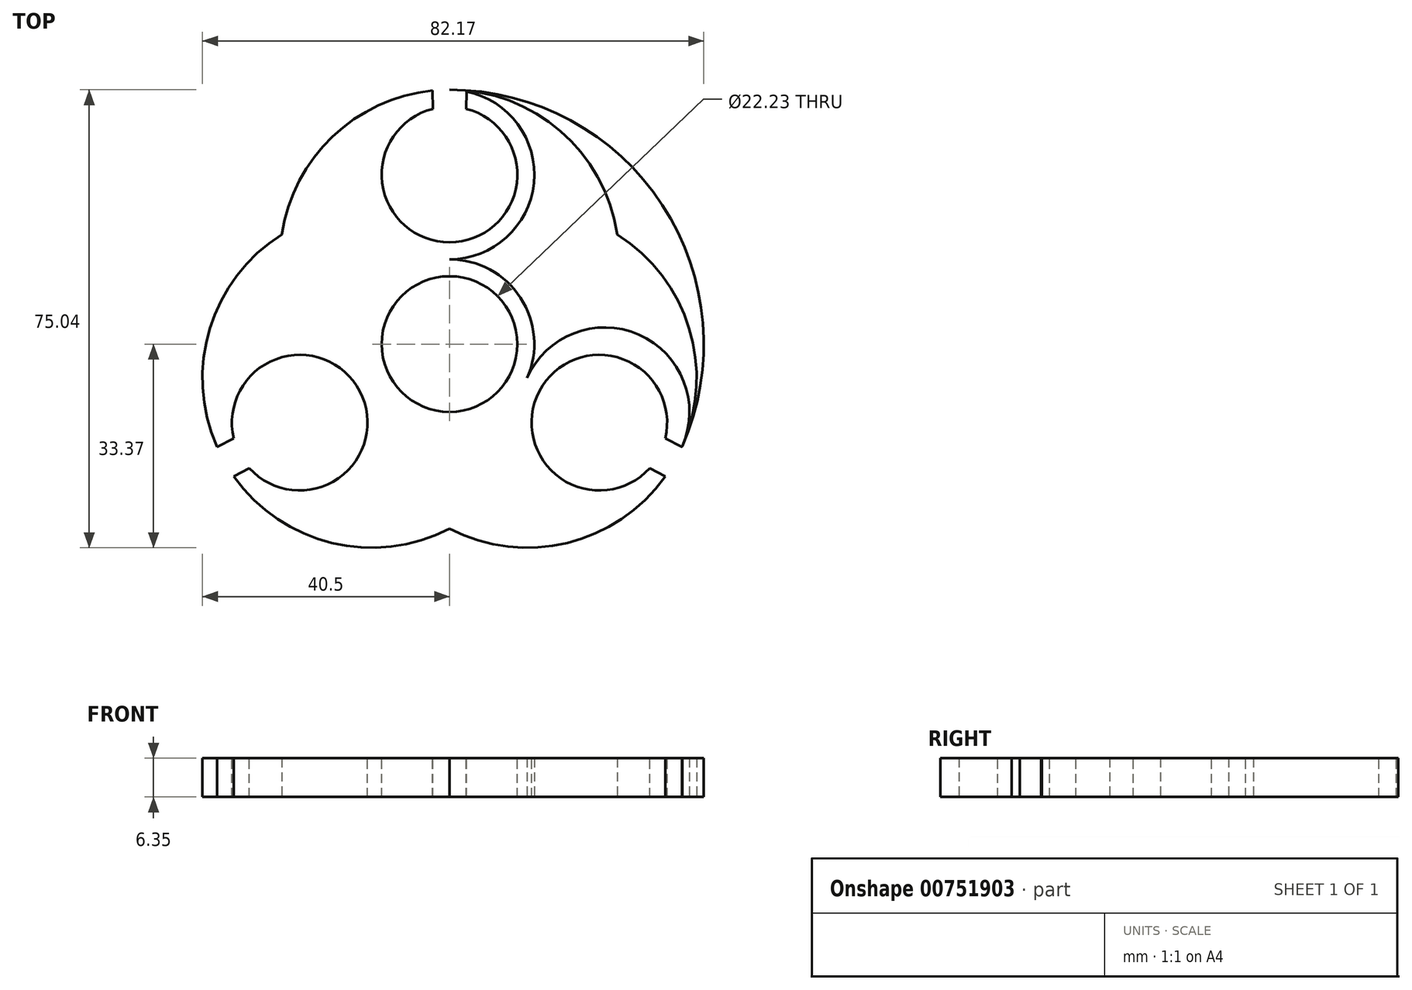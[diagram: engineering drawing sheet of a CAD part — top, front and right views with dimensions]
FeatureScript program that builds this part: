
annotation { "Feature Type Name" : "Feature", "Feature Type Description" : "" }
export const myFeature = defineFeature(function(context is Context, id is Id, definition is map)
    precondition{}
    {
        {
            var Q0;
            Q0=qCreatedBy(makeId("Top.planeOp"),FACE);
            var sketch = newSketch(context, id + "F0", { "sketchPlane" : qUnion([Q0])});
            skCircle(sketch, "E0", {"center": v(0, 0) * mm, "radius": 13.9 * mm});
            skCircle(sketch, "E1", {"center": v(0, 27.78) * mm, "radius": 13.9 * mm});
            skArc(sketch, "E2", {"start": v(0, 41.67) * mm, "mid": v(34.89, 22.79) * mm, "end": v(38.16, -16.75) * mm});
            skArc(sketch, "E3", {"start": v(38.16, -16.75) * mm, "mid": v(0, -41.67) * mm, "end": v(-38.16, -16.75) * mm});
            skArc(sketch, "E4", {"start": v(-38.16, -16.75) * mm, "mid": v(-34.89, 22.79) * mm, "end": v(0, 41.67) * mm});
            skCircle(sketch, "E5", {"center": v(25.44, -11.17) * mm, "radius": 13.9 * mm});
            skCircle(sketch, "E6", {"center": v(-25.44, -11.17) * mm, "radius": 13.9 * mm});
            skArc(sketch, "E7", {"start": v(0, 41.67) * mm, "mid": v(18.15, 34.92) * mm, "end": v(27.48, 17.95) * mm});
            skArc(sketch, "E8", {"start": v(0, 41.67) * mm, "mid": v(-18.15, 34.92) * mm, "end": v(-27.48, 17.95) * mm});
            skArc(sketch, "E9", {"start": v(-38.16, -16.75) * mm, "mid": v(-39.27, 2.58) * mm, "end": v(-27.48, 17.95) * mm});
            skArc(sketch, "E10", {"start": v(-38.16, -16.75) * mm, "mid": v(-22, -31.77) * mm, "end": v(0, -30.28) * mm});
            skArc(sketch, "E11", {"start": v(0, -30.28) * mm, "mid": v(22, -31.77) * mm, "end": v(38.16, -16.75) * mm});
            skArc(sketch, "E12", {"start": v(38.16, -16.75) * mm, "mid": v(39.27, 2.58) * mm, "end": v(27.48, 17.95) * mm});
            skSolve(sketch);
        }
        {
            var Q0;
            {var subQ0=sQuery(id+"F0.wireOp",EDGE,"E5");var subQ2=makeQuery(id+"F0.imprint","INTERSECT",VERTEX,{"derivedFrom":[sQuery(id+"F0.wireOp",EDGE,"E0"),subQ0]});Q0=makeQuery(id+"F0.imprint","IMPRINT",FACE,{"disambiguationData":[TD([[makeQuery(id+"F0.imprint","IMPRINT",EDGE,{"disambiguationData":[TD([[subQ2,-1.0]])],"derivedFrom":subQ0}),1.0]])]});}
            var Q1;
            {var subQ0=sQuery(id+"F0.wireOp",EDGE,"E8");Q1=makeQuery(id+"F0.imprint","IMPRINT",FACE,{"disambiguationData":[TD([[makeQuery(id+"F0.imprint","IMPRINT",EDGE,{"derivedFrom":subQ0}),1.0]])]});}
            var Q2;
            {var subQ0=sQuery(id+"F0.wireOp",EDGE,"E10");Q2=makeQuery(id+"F0.imprint","IMPRINT",FACE,{"disambiguationData":[TD([[makeQuery(id+"F0.imprint","IMPRINT",EDGE,{"derivedFrom":subQ0}),1.0]])]});}
            var Q3;
            {var subQ5=sQuery(id+"F0.wireOp",EDGE,"E7");Q3=makeQuery(id+"F0.imprint","IMPRINT",FACE,{"disambiguationData":[TD([[makeQuery(id+"F0.imprint","IMPRINT",EDGE,{"derivedFrom":subQ5}),-1.0]])]});}
            var Q4;
            {var subQ0=sQuery(id+"F0.wireOp",EDGE,"E6");var subQ2=makeQuery(id+"F0.imprint","INTERSECT",VERTEX,{"derivedFrom":[sQuery(id+"F0.wireOp",EDGE,"E0"),subQ0]});Q4=makeQuery(id+"F0.imprint","IMPRINT",FACE,{"disambiguationData":[TD([[makeQuery(id+"F0.imprint","IMPRINT",EDGE,{"disambiguationData":[TD([[subQ2,-1.0]])],"derivedFrom":subQ0}),1.0]])]});}
            var Q5;
            {var subQ0=sQuery(id+"F0.wireOp",EDGE,"E0");var subQ1=makeQuery(id+"F0.imprint","INTERSECT",VERTEX,{"derivedFrom":[subQ0,sQuery(id+"F0.wireOp",EDGE,"E6")]});Q5=makeQuery(id+"F0.imprint","IMPRINT",FACE,{"disambiguationData":[TD([[makeQuery(id+"F0.imprint","IMPRINT",EDGE,{"disambiguationData":[TD([[subQ1,1.0]])],"derivedFrom":subQ0}),1.0]])]});}
            var Q6;
            {var subQ0=sQuery(id+"F0.wireOp",EDGE,"E1");var subQ2=makeQuery(id+"F0.imprint","INTERSECT",VERTEX,{"derivedFrom":[sQuery(id+"F0.wireOp",EDGE,"E0"),subQ0]});Q6=makeQuery(id+"F0.imprint","IMPRINT",FACE,{"disambiguationData":[TD([[makeQuery(id+"F0.imprint","IMPRINT",EDGE,{"disambiguationData":[TD([[subQ2,1.0]])],"derivedFrom":subQ0}),1.0]])]});}
            extrude(context, id + "F1", {"entities" : qUnion([Q0, Q1, Q2, Q3, Q4, Q5, Q6]), "depth" : 6.35 * mm, "offsetDistance" : 25.4 * mm});
        }
        {
            var Q0;
            Q0=makeQuery(id+"F1.opExtrude","CAP_FACE",FACE,{"disambiguationData":[OSD([sQuery(id+"F0.wireOp",EDGE,"E7"),sQuery(id+"F0.wireOp",EDGE,"E8"),sQuery(id+"F0.wireOp",EDGE,"E9"),sQuery(id+"F0.wireOp",EDGE,"E10"),sQuery(id+"F0.wireOp",EDGE,"E11"),sQuery(id+"F0.wireOp",EDGE,"E12")])],"isStart":false});
            var sketch = newSketch(context, id + "F2", { "sketchPlane" : qUnion([Q0])});
            skCircle(sketch, "E13", {"center": v(0, 0) * mm, "radius": 11.11 * mm});
            skLineSegment(sketch, "E14", {"start": v(0, 41.67) * mm, "end": v(0, 27.78) * mm});
            skLineSegment(sketch, "E15", {"start": v(36.86, -19.34) * mm, "end": v(24.56, -12.88) * mm});
            skLineSegment(sketch, "E16", {"start": v(-36.86, -19.34) * mm, "end": v(-24.56, -12.88) * mm});
            skCircle(sketch, "E17", {"center": v(0, 27.78) * mm, "radius": 11.11 * mm});
            skCircle(sketch, "E18", {"center": v(-24.56, -12.88) * mm, "radius": 11.11 * mm});
            skCircle(sketch, "E19", {"center": v(24.56, -12.88) * mm, "radius": 11.11 * mm});
            skLineSegment(sketch, "E20", {"start": v(35.37, -15.44) * mm, "end": v(38.1, -16.86) * mm});
            skLineSegment(sketch, "E21", {"start": v(32.8, -20.33) * mm, "end": v(35.36, -21.68) * mm});
            skLineSegment(sketch, "E22", {"start": v(-38.1, -16.86) * mm, "end": v(-35.37, -15.44) * mm});
            skLineSegment(sketch, "E23", {"start": v(-35.36, -21.68) * mm, "end": v(-32.8, -20.33) * mm});
            skLineSegment(sketch, "E24", {"start": v(-2.76, 38.55) * mm, "end": v(-2.77, 41.53) * mm});
            skLineSegment(sketch, "E25", {"start": v(2.77, 41.53) * mm, "end": v(2.76, 38.55) * mm});
            skSolve(sketch);
        }
        {
            var Q0;
            Q0=qSketchRegion(id+"F2",true);
            var Q1;
            {var subQ5=sQuery(id+"F2.wireOp",EDGE,"E24");Q1=makeQuery(id+"F2.imprint","IMPRINT",FACE,{"disambiguationData":[TD([[makeQuery(id+"F2.imprint","IMPRINT",EDGE,{"derivedFrom":subQ5}),-1.0]])]});}
            var Q2;
            {var subQ5=sQuery(id+"F2.wireOp",EDGE,"E25");Q2=makeQuery(id+"F2.imprint","IMPRINT",FACE,{"disambiguationData":[TD([[makeQuery(id+"F2.imprint","IMPRINT",EDGE,{"derivedFrom":subQ5}),-1.0]])]});}
            var Q3;
            {var subQ5=sQuery(id+"F2.wireOp",EDGE,"E21");Q3=makeQuery(id+"F2.imprint","IMPRINT",FACE,{"disambiguationData":[TD([[makeQuery(id+"F2.imprint","IMPRINT",EDGE,{"derivedFrom":subQ5}),1.0]])]});}
            var Q4;
            {var subQ5=sQuery(id+"F2.wireOp",EDGE,"E20");Q4=makeQuery(id+"F2.imprint","IMPRINT",FACE,{"disambiguationData":[TD([[makeQuery(id+"F2.imprint","IMPRINT",EDGE,{"derivedFrom":subQ5}),-1.0]])]});}
            var Q5;
            {var subQ5=sQuery(id+"F2.wireOp",EDGE,"E23");Q5=makeQuery(id+"F2.imprint","IMPRINT",FACE,{"disambiguationData":[TD([[makeQuery(id+"F2.imprint","IMPRINT",EDGE,{"derivedFrom":subQ5}),1.0]])]});}
            var Q6;
            {var subQ5=sQuery(id+"F2.wireOp",EDGE,"E22");Q6=makeQuery(id+"F2.imprint","IMPRINT",FACE,{"disambiguationData":[TD([[makeQuery(id+"F2.imprint","IMPRINT",EDGE,{"derivedFrom":subQ5}),-1.0]])]});}
            extrude(context, id + "F3", {"entities" : qUnion([Q0, Q1, Q2, Q3, Q4, Q5, Q6]), "operationType" : NewBodyOperationType.REMOVE, "oppositeDirection" : true, "depth" : 25.4 * mm, "offsetDistance" : 25.4 * mm});
        }
    });
